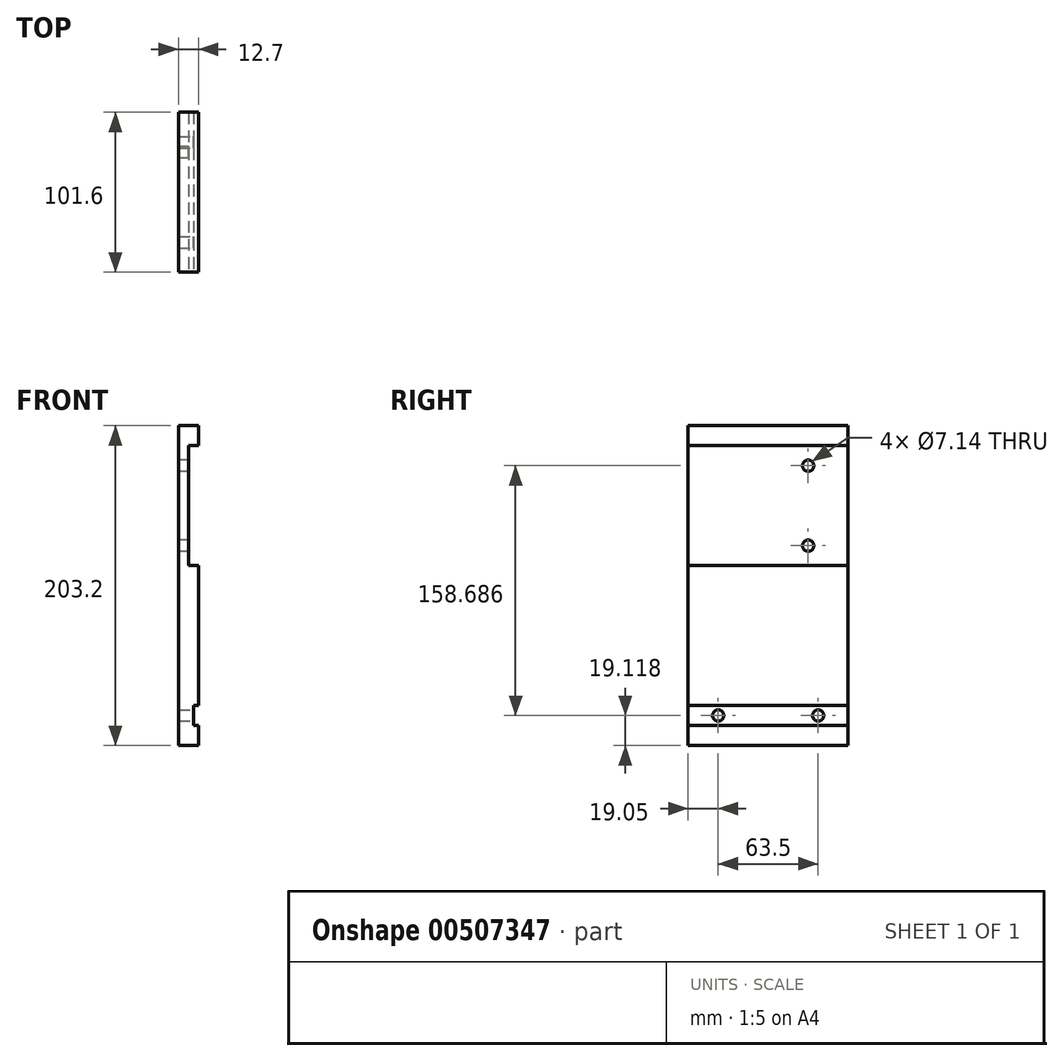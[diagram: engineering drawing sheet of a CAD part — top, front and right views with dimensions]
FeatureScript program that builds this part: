
annotation { "Feature Type Name" : "Feature", "Feature Type Description" : "" }
export const myFeature = defineFeature(function(context is Context, id is Id, definition is map)
    precondition{}
    {
        {
            var Q0;
            Q0=qCreatedBy(makeId("Front.planeOp"),FACE);
            var sketch = newSketch(context, id + "F0", { "sketchPlane" : qUnion([Q0])});
            skLineSegment(sketch, "E0", {"start": v(-57.91, 44.36) * mm, "end": v(-57.91, -158.84) * mm});
            skLineSegment(sketch, "E1", {"start": v(-57.91, -158.84) * mm, "end": v(-45.21, -158.84) * mm});
            skLineSegment(sketch, "E2", {"start": v(-45.21, -158.84) * mm, "end": v(-45.21, 44.36) * mm});
            skLineSegment(sketch, "E3", {"start": v(-57.91, 44.36) * mm, "end": v(-45.21, 44.36) * mm});
            skSolve(sketch);
        }
        {
            var Q0;
            Q0 = qSketchRegion(id + "F0", true);
            extrude(context, id + "F1", {"entities" : qUnion([Q0]), "depth" : 101.6 * mm});
        }
        {
            var Q0;
            Q0=makeQuery(id+"F1.opExtrude","CAP_FACE",FACE,{"disambiguationData":[OSD([sQuery(id+"F0.wireOp",EDGE,"E0"),sQuery(id+"F0.wireOp",EDGE,"E1"),sQuery(id+"F0.wireOp",EDGE,"E2"),sQuery(id+"F0.wireOp",EDGE,"E3")])],"isStart":false});
            var sketch = newSketch(context, id + "F2", { "sketchPlane" : qUnion([Q0])});
            skLineSegment(sketch, "E4", {"start": v(-45.21, -133.3) * mm, "end": v(-48.39, -133.3) * mm});
            skLineSegment(sketch, "E5", {"start": v(-48.39, -133.3) * mm, "end": v(-48.39, -146.14) * mm});
            skLineSegment(sketch, "E6", {"start": v(-48.39, -146.14) * mm, "end": v(-45.21, -146.14) * mm});
            skLineSegment(sketch, "E7", {"start": v(-45.21, -146.14) * mm, "end": v(-45.21, -133.3) * mm});
            skSolve(sketch);
        }
        {
            var Q0;
            Q0=makeQuery(id+"F2.imprint","IMPRINT",FACE,{"disambiguationData":[TD([[makeQuery(id+"F2.imprint","IMPRINT",EDGE,{"derivedFrom":sQuery(id+"F2.wireOp",EDGE,"E4")}),1.0]])]});
            extrude(context, id + "F3", {"entities" : qUnion([Q0]), "operationType" : NewBodyOperationType.REMOVE, "endBound" : BoundingType.UP_TO_NEXT, "oppositeDirection" : true, "depth" : 25.4 * mm});
        }
        {
            var Q0;
            Q0=makeQuery(id+"F3.boolean.opBoolean","COPY",FACE,{"derivedFrom":makeQuery(id+"F3.opExtrude","SWEPT_FACE",FACE,{"disambiguationData":[OSD([sQuery(id+"F2.wireOp",EDGE,"E5")])]})});
            var sketch = newSketch(context, id + "F4", { "sketchPlane" : qUnion([Q0])});
            skCircle(sketch, "E8", {"center": v(-82.55, -139.72) * mm, "radius": 3.57 * mm});
            skCircle(sketch, "E9", {"center": v(-19.05, -139.72) * mm, "radius": 3.57 * mm});
            skSolve(sketch);
        }
        {
            var Q0;
            Q0 = qSketchRegion(id + "F4", true);
            extrude(context, id + "F5", {"entities" : qUnion([Q0]), "operationType" : NewBodyOperationType.REMOVE, "endBound" : BoundingType.UP_TO_NEXT, "oppositeDirection" : true, "depth" : 25.4 * mm});
        }
        {
            var Q0;
            Q0=makeQuery(id+"F1.opExtrude","CAP_FACE",FACE,{"disambiguationData":[OSD([sQuery(id+"F0.wireOp",EDGE,"E0"),sQuery(id+"F0.wireOp",EDGE,"E1"),sQuery(id+"F0.wireOp",EDGE,"E2"),sQuery(id+"F0.wireOp",EDGE,"E3")])],"isStart":false});
            var sketch = newSketch(context, id + "F6", { "sketchPlane" : qUnion([Q0])});
            skLineSegment(sketch, "E10", {"start": v(-45.21, 31.66) * mm, "end": v(-51.56, 31.66) * mm});
            skLineSegment(sketch, "E11", {"start": v(-51.56, 31.66) * mm, "end": v(-51.56, -44.54) * mm});
            skLineSegment(sketch, "E12", {"start": v(-51.56, -44.54) * mm, "end": v(-45.21, -44.54) * mm});
            skLineSegment(sketch, "E13", {"start": v(-45.21, -44.54) * mm, "end": v(-45.21, 31.66) * mm});
            skSolve(sketch);
        }
        {
            var Q0;
            Q0 = qSketchRegion(id + "F6", true);
            extrude(context, id + "F7", {"entities" : qUnion([Q0]), "operationType" : NewBodyOperationType.REMOVE, "endBound" : BoundingType.UP_TO_NEXT, "oppositeDirection" : true, "depth" : 25.4 * mm});
        }
        {
            var Q0;
            Q0=makeQuery(id+"F1.opExtrude","SWEPT_FACE",FACE,{"disambiguationData":[OSD([sQuery(id+"F0.wireOp",EDGE,"E0")])]});
            var sketch = newSketch(context, id + "F8", { "sketchPlane" : qUnion([Q0])});
            skCircle(sketch, "E14", {"center": v(25.4, 18.96) * mm, "radius": 3.57 * mm});
            skCircle(sketch, "E15", {"center": v(25.4, -31.84) * mm, "radius": 3.57 * mm});
            skSolve(sketch);
        }
        {
            var Q0;
            Q0 = qSketchRegion(id + "F8", true);
            extrude(context, id + "F9", {"entities" : qUnion([Q0]), "operationType" : NewBodyOperationType.REMOVE, "endBound" : BoundingType.UP_TO_NEXT, "oppositeDirection" : true, "depth" : 25.4 * mm});
        }
    });
